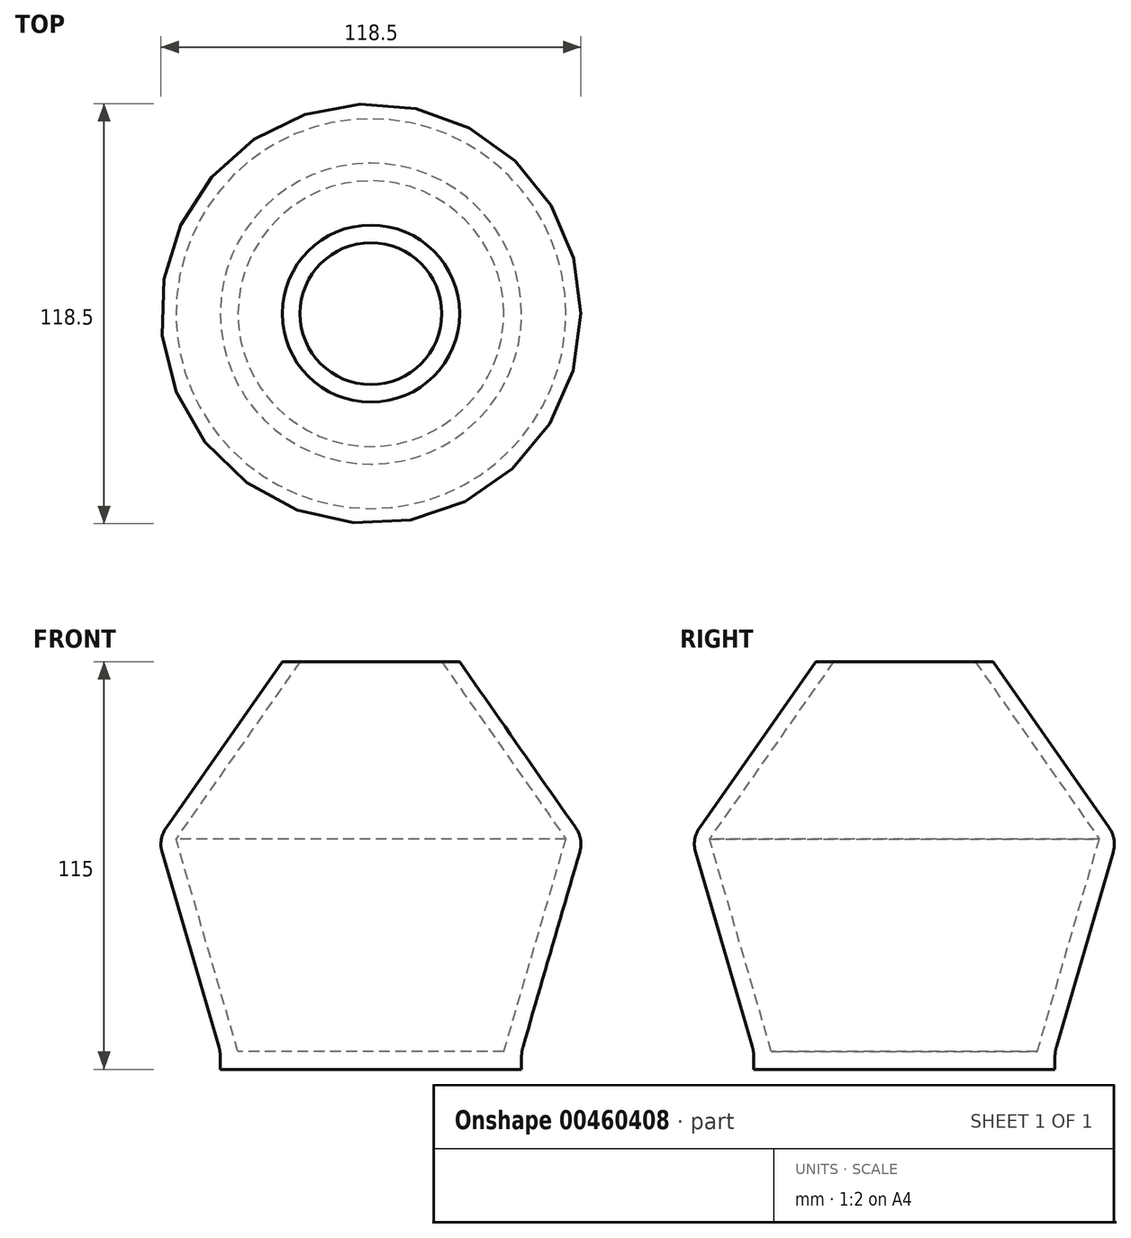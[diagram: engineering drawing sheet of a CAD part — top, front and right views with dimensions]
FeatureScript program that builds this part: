
annotation { "Feature Type Name" : "Feature", "Feature Type Description" : "" }
export const myFeature = defineFeature(function(context is Context, id is Id, definition is map)
    precondition{}
    {
        {
            var Q0;
            Q0=qCreatedBy(makeId("Top.planeOp"),FACE);
            cPlane(context, id + "F0", {"entities" : qUnion([Q0]), "cplaneType" : CPlaneType.OFFSET, "offset" : 50 * mm, "width" : 150 * mm, "height" : 150 * mm});
        }
        {
            var Q0;
            Q0=qCreatedBy(makeId("Top.planeOp"),FACE);
            var sketch = newSketch(context, id + "F1", { "sketchPlane" : qUnion([Q0])});
            skCircle(sketch, "E0", {"center": v(0, 0) * mm, "radius": 60 * mm});
            skSolve(sketch);
        }
        {
            var Q0;
            Q0=qCreatedBy(id+"F0.planeOp",FACE);
            var sketch = newSketch(context, id + "F2", { "sketchPlane" : qUnion([Q0])});
            skCircle(sketch, "E1", {"center": v(0, 0) * mm, "radius": 25 * mm});
            skSolve(sketch);
        }
        {
            var Q0;
            Q0=makeQuery(id+"F2.imprint","IMPRINT",FACE,{"disambiguationData":[TD([[makeQuery(id+"F2.imprint","IMPRINT",EDGE,{"derivedFrom":sQuery(id+"F2.wireOp",EDGE,"E1")}),1.0]])]});
            var Q1;
            Q1=makeQuery(id+"F1.imprint","IMPRINT",FACE,{"disambiguationData":[TD([[makeQuery(id+"F1.imprint","IMPRINT",EDGE,{"derivedFrom":sQuery(id+"F1.wireOp",EDGE,"E0")}),1.0]])]});
            loft(context, id + "F3", {"sheetProfilesArray" : [{ "sheetProfileEntities" : qUnion([Q0]) }, { "sheetProfileEntities" : qUnion([Q1]) }]});
        }
        {
            var Q0;
            Q0=qCreatedBy(makeId("Top.planeOp"),FACE);
            cPlane(context, id + "F4", {"entities" : qUnion([Q0]), "cplaneType" : CPlaneType.OFFSET, "offset" : 60 * mm, "oppositeDirection" : true, "width" : 150 * mm, "height" : 150 * mm});
        }
        {
            var Q0;
            Q0=qCreatedBy(id+"F4.planeOp",FACE);
            var sketch = newSketch(context, id + "F5", { "sketchPlane" : qUnion([Q0])});
            skCircle(sketch, "E2", {"center": v(0, 0) * mm, "radius": 42.5 * mm});
            skSolve(sketch);
        }
        {
            var Q1;
            Q1=makeQuery(id+"F5.imprint","IMPRINT",FACE,{"disambiguationData":[TD([[makeQuery(id+"F5.imprint","IMPRINT",EDGE,{"derivedFrom":sQuery(id+"F5.wireOp",EDGE,"E2")}),1.0]])]});
            var Q2;
            Q2=makeQuery(id+"F3.opLoft","CAP_FACE",FACE,{"disambiguationData":[OSD([makeQuery(id+"F1.imprint","IMPRINT",FACE,{"disambiguationData":[TD([[makeQuery(id+"F1.imprint","IMPRINT",EDGE,{"derivedFrom":sQuery(id+"F1.wireOp",EDGE,"E0")}),1.0]])]})])],"isStart":true});
            loft(context, id + "F6", {"operationType" : NewBodyOperationType.ADD, "sheetProfilesArray" : [{ "sheetProfileEntities" : qUnion([Q1]) }, { "sheetProfileEntities" : qUnion([Q2]) }]});
        }
        {
            var Q0;
            Q0=qCreatedBy(id+"F0.planeOp",FACE);
            var sketch = newSketch(context, id + "F7", { "sketchPlane" : qUnion([Q0])});
            skCircle(sketch, "E3", {"center": v(0, 0) * mm, "radius": 20 * mm});
            skSolve(sketch);
        }
        {
            var Q0;
            Q0=qCreatedBy(id+"F4.planeOp",FACE);
            var sketch = newSketch(context, id + "F8", { "sketchPlane" : qUnion([Q0])});
            skCircle(sketch, "E4", {"center": v(0, 0) * mm, "radius": 37.5 * mm});
            skSolve(sketch);
        }
        {
            var Q0;
            Q0=qCreatedBy(makeId("Top.planeOp"),FACE);
            var sketch = newSketch(context, id + "F9", { "sketchPlane" : qUnion([Q0])});
            skCircle(sketch, "E5", {"center": v(0, 0) * mm, "radius": 55 * mm});
            skSolve(sketch);
        }
        {
            var Q1;
            Q1 = qSketchRegion(id + "F9", true);
            var Q2;
            Q2=makeQuery(id+"F7.imprint","IMPRINT",FACE,{"disambiguationData":[TD([[makeQuery(id+"F7.imprint","IMPRINT",EDGE,{"derivedFrom":sQuery(id+"F7.wireOp",EDGE,"E3")}),1.0]])]});
            loft(context, id + "F10", {"operationType" : NewBodyOperationType.REMOVE, "sheetProfilesArray" : [{ "sheetProfileEntities" : qUnion([Q1]) }, { "sheetProfileEntities" : qUnion([Q2]) }]});
        }
        {
            var Q1;
            Q1 = qSketchRegion(id + "F8", true);
            var Q2;
            Q2 = qSketchRegion(id + "F9", true);
            loft(context, id + "F11", {"operationType" : NewBodyOperationType.REMOVE, "sheetProfilesArray" : [{ "sheetProfileEntities" : qUnion([Q1]) }, { "sheetProfileEntities" : qUnion([Q2]) }]});
        }
        {
            var Q0;
            {var subQ0=sQuery(id+"F2.wireOp",EDGE,"E1");var subQ1=sQuery(id+"F1.wireOp",EDGE,"E0");Q0=makeQuery(id+"F6.boolean.opBoolean","MERGE",EDGE,{"derivedFrom":[makeQuery(id+"F3.opLoft","MID_CAP_EDGE",EDGE,{"disambiguationData":[OSD([subQ1,subQ0])],"capPos":1.0}),makeQuery(id+"F6.opLoft","MID_CAP_EDGE",EDGE,{"disambiguationData":[OSD([subQ1,subQ0,sQuery(id+"F5.wireOp",EDGE,"E2")])],"capPos":1.0})]});}
            fillet(context, id + "F12", {"entities" : qUnion([Q0]), "radius" : 8 * mm, "tangentPropagation" : true, "allowEdgeOverflow" : false});
        }
        {
            var Q0;
            Q0=qCreatedBy(id+"F4.planeOp",FACE);
            var sketch = newSketch(context, id + "F13", { "sketchPlane" : qUnion([Q0])});
            skCircle(sketch, "E6", {"center": v(0, 0) * mm, "radius": 42.5 * mm});
            skSolve(sketch);
        }
        {
            var Q0;
            Q0 = qSketchRegion(id + "F13", true);
            extrude(context, id + "F14", {"entities" : qUnion([Q0]), "operationType" : NewBodyOperationType.ADD, "oppositeDirection" : true, "depth" : 5 * mm});
        }
        {
            var Q0;
            Q0=makeQuery(id+"F14.boolean.opBoolean","MERGE",EDGE,{"derivedFrom":[makeQuery(id+"F6.opLoft","MID_CAP_EDGE",EDGE,{"disambiguationData":[OSD([sQuery(id+"F5.wireOp",EDGE,"E2")])],"capPos":0.0}),makeQuery(id+"F14.opExtrude","CAP_EDGE",EDGE,{"disambiguationData":[OSD([sQuery(id+"F13.wireOp",EDGE,"E6")])],"isStart":true})]});
            fillet(context, id + "F15", {"entities" : qUnion([Q0]), "radius" : 10 * mm, "tangentPropagation" : true, "allowEdgeOverflow" : false});
        }
        {
            var Q0;
            Q0=qCreatedBy(makeId("Front.planeOp"),FACE);
            var sketch = newSketch(context, id + "F16", { "sketchPlane" : qUnion([Q0])});
            skLineSegment(sketch, "E7", {"start": v(24.65, 51.43) * mm, "end": v(59.5, 0) * mm});
            skSolve(sketch);
        }
    });
